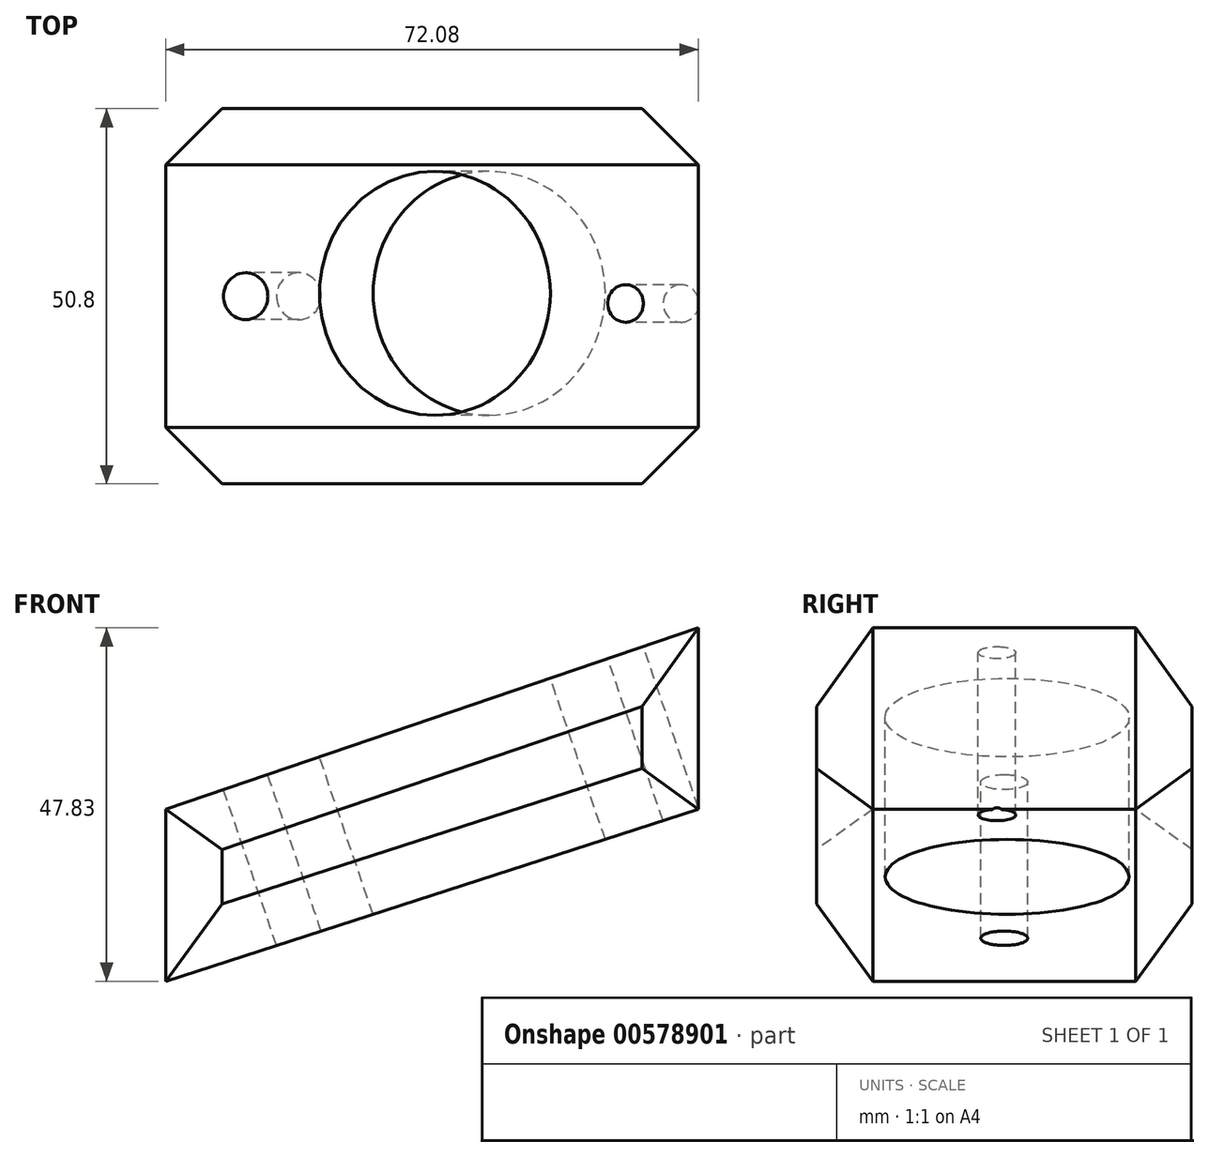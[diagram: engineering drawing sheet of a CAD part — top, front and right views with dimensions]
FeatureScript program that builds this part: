
annotation { "Feature Type Name" : "Feature", "Feature Type Description" : "" }
export const myFeature = defineFeature(function(context is Context, id is Id, definition is map)
    precondition{}
    {
        {
            var Q0;
            Q0=qCreatedBy(makeId("Front.planeOp"),FACE);
            var sketch = newSketch(context, id + "F0", { "sketchPlane" : qUnion([Q0])});
            skLineSegment(sketch, "E0", {"start": v(0, 0) * mm, "end": v(0, -23.26) * mm});
            skLineSegment(sketch, "E1", {"start": v(0, -23.26) * mm, "end": v(72.08, 0) * mm});
            skLineSegment(sketch, "E2", {"start": v(72.08, 0) * mm, "end": v(72.08, 24.57) * mm});
            skLineSegment(sketch, "E3", {"start": v(72.08, 24.57) * mm, "end": v(0, 0) * mm});
            skSolve(sketch);
        }
        {
            var Q0;
            Q0=makeQuery(id+"F0.imprint","IMPRINT",FACE,{"disambiguationData":[TD([[makeQuery(id+"F0.imprint","IMPRINT",EDGE,{"derivedFrom":sQuery(id+"F0.wireOp",EDGE,"E0")}),1.0]])]});
            extrude(context, id + "F1", {"entities" : qUnion([Q0]), "depth" : 50.8 * mm, "offsetDistance" : 25.4 * mm});
        }
        {
            var Q0;
            Q0=makeQuery(id+"F1.opExtrude","SWEPT_FACE",FACE,{"disambiguationData":[OSD([sQuery(id+"F0.wireOp",EDGE,"E3")])]});
            var sketch = newSketch(context, id + "F2", { "sketchPlane" : qUnion([Q0])});
            skPoint(sketch, "E4", {"position": v(38.5, -25) * mm});
            skSolve(sketch);
        }
        {
            var Q0;
            Q0=sQuery(id+"F2.wireOp",VERTEX,"E4");
            var Q1;
            Q1=makeQuery(id+"F1.opExtrude","SWEPT_BODY",BODY,{"disambiguationData":[OSD([sQuery(id+"F0.wireOp",EDGE,"E0"),sQuery(id+"F0.wireOp",EDGE,"E1"),sQuery(id+"F0.wireOp",EDGE,"E2"),sQuery(id+"F0.wireOp",EDGE,"E3")])]});
            hole(context, id + "F3", {"style" : HoleStyle.SIMPLE, "endStyle" : HoleEndStyle.THROUGH, "holeDiameter" : 33.02 * mm, "isTappedThrough" : true, "tappedDepth" : 12.7 * mm, "tapClearance" : 3, "locations" : qUnion([Q0]), "scope" : qUnion([Q1])});
        }
        {
            var Q0;
            Q0=makeQuery(id+"F1.opExtrude","CAP_FACE",FACE,{"disambiguationData":[OSD([sQuery(id+"F0.wireOp",EDGE,"E0"),sQuery(id+"F0.wireOp",EDGE,"E1"),sQuery(id+"F0.wireOp",EDGE,"E2"),sQuery(id+"F0.wireOp",EDGE,"E3")])],"isStart":false});
            chamfer(context, id + "F4", {"entities" : qUnion([Q0]), "width" : 7.62 * mm, "tangentPropagation" : true});
        }
        {
            var Q0;
            Q0=makeQuery(id+"F1.opExtrude","CAP_FACE",FACE,{"disambiguationData":[OSD([sQuery(id+"F0.wireOp",EDGE,"E0"),sQuery(id+"F0.wireOp",EDGE,"E1"),sQuery(id+"F0.wireOp",EDGE,"E2"),sQuery(id+"F0.wireOp",EDGE,"E3")])],"isStart":true});
            chamfer(context, id + "F5", {"entities" : qUnion([Q0]), "width" : 7.62 * mm, "tangentPropagation" : true});
        }
        {
            var Q0;
            Q0=makeQuery(id+"F1.opExtrude","SWEPT_FACE",FACE,{"disambiguationData":[OSD([sQuery(id+"F0.wireOp",EDGE,"E3")])]});
            var sketch = newSketch(context, id + "F6", { "sketchPlane" : qUnion([Q0])});
            skPoint(sketch, "E5", {"position": v(65.76, -26.37) * mm});
            skSolve(sketch);
        }
        {
            var Q0;
            Q0=sQuery(id+"F6.wireOp",VERTEX,"E5");
            var Q1;
            Q1=makeQuery(id+"F1.opExtrude","SWEPT_BODY",BODY,{"disambiguationData":[OSD([sQuery(id+"F0.wireOp",EDGE,"E0"),sQuery(id+"F0.wireOp",EDGE,"E1"),sQuery(id+"F0.wireOp",EDGE,"E2"),sQuery(id+"F0.wireOp",EDGE,"E3")])]});
            hole(context, id + "F7", {"style" : HoleStyle.SIMPLE, "endStyle" : HoleEndStyle.THROUGH, "holeDiameter" : 5.08 * mm, "isTappedThrough" : true, "tappedDepth" : 12.7 * mm, "tapClearance" : 3, "locations" : qUnion([Q0]), "scope" : qUnion([Q1])});
        }
        {
            var Q0;
            Q0=makeQuery(id+"F1.opExtrude","SWEPT_FACE",FACE,{"disambiguationData":[OSD([sQuery(id+"F0.wireOp",EDGE,"E3")])]});
            var sketch = newSketch(context, id + "F8", { "sketchPlane" : qUnion([Q0])});
            skPoint(sketch, "E6", {"position": v(11.44, -25.4) * mm});
            skPoint(sketch, "E6.positionSnap0", {"position": v(0, -25.4) * mm});
            skSolve(sketch);
        }
        {
            var Q0;
            Q0=sQuery(id+"F8.wireOp",VERTEX,"E6");
            var Q1;
            Q1=makeQuery(id+"F1.opExtrude","SWEPT_BODY",BODY,{"disambiguationData":[OSD([sQuery(id+"F0.wireOp",EDGE,"E0"),sQuery(id+"F0.wireOp",EDGE,"E1"),sQuery(id+"F0.wireOp",EDGE,"E2"),sQuery(id+"F0.wireOp",EDGE,"E3")])]});
            hole(context, id + "F9", {"style" : HoleStyle.SIMPLE, "endStyle" : HoleEndStyle.THROUGH, "holeDiameter" : 6.35 * mm, "isTappedThrough" : true, "tappedDepth" : 12.7 * mm, "tapClearance" : 3, "locations" : qUnion([Q0]), "scope" : qUnion([Q1])});
        }
    });
